# Revit family: Erdungs-System_isFang_isolierter_Fangmast_für_innenverlegte_isCon-Leitung_mit_seitlichem_Auslass
name_source: partatom
category: Generic Models
revit_build: Autodesk Revit 2015 (Build: 20140606_1530(x64)
units: mm (PartAtom-declared; Revit-internal decimal feet)

## types (4) — shared parameters
Manufacturer = OBO Bettermann
Material = GFRP
URL = http://www.obo-bettermann.com

## per-type parameters (varying)
| type | A | B | GTIN | H | L | Manufacturer Art. No. |
| isFang IN-A 8000 | 5335 mm  [stored 17.5033 ft] | 1000 mm  [stored 3.28084 ft] | 4012196219414 | 1500 mm  [stored 4.92126 ft] | 8000 mm  [stored 26.2467 ft] | 5408888 |
| isFang IN-A 4000 | 1325 mm  [stored 4.34711 ft] | 1000 mm  [stored 3.28084 ft] | 4012195871668 | 1500 mm  [stored 4.92126 ft] | 4000 mm  [stored 13.1234 ft] | 5408938 |
| isFang IN-A 6000 | 3325 mm  [stored 10.9088 ft] | 1000 mm  [stored 3.28084 ft] | 4012195871675 | 1500 mm  [stored 4.92126 ft] | 6000 mm  [stored 19.685 ft] | 5408940 |
| isFang IN-A 10000 | 6000 mm  [stored 19.685 ft] | 2000 mm  [stored 6.56168 ft] | 4012196219421 | 1733 mm  [stored 5.6857 ft] | 10000 mm  [stored 32.8084 ft] | 5408890 |

note: column(s) folded — value = type name in every type: Article Type

note: [stored X ft] marks values corroborated as IEEE doubles in the binary element streams (Revit-internal decimal feet)

## geometry (parser evidence)
native form markers: Sweep x2
no freeform markers — native parametric forms only
